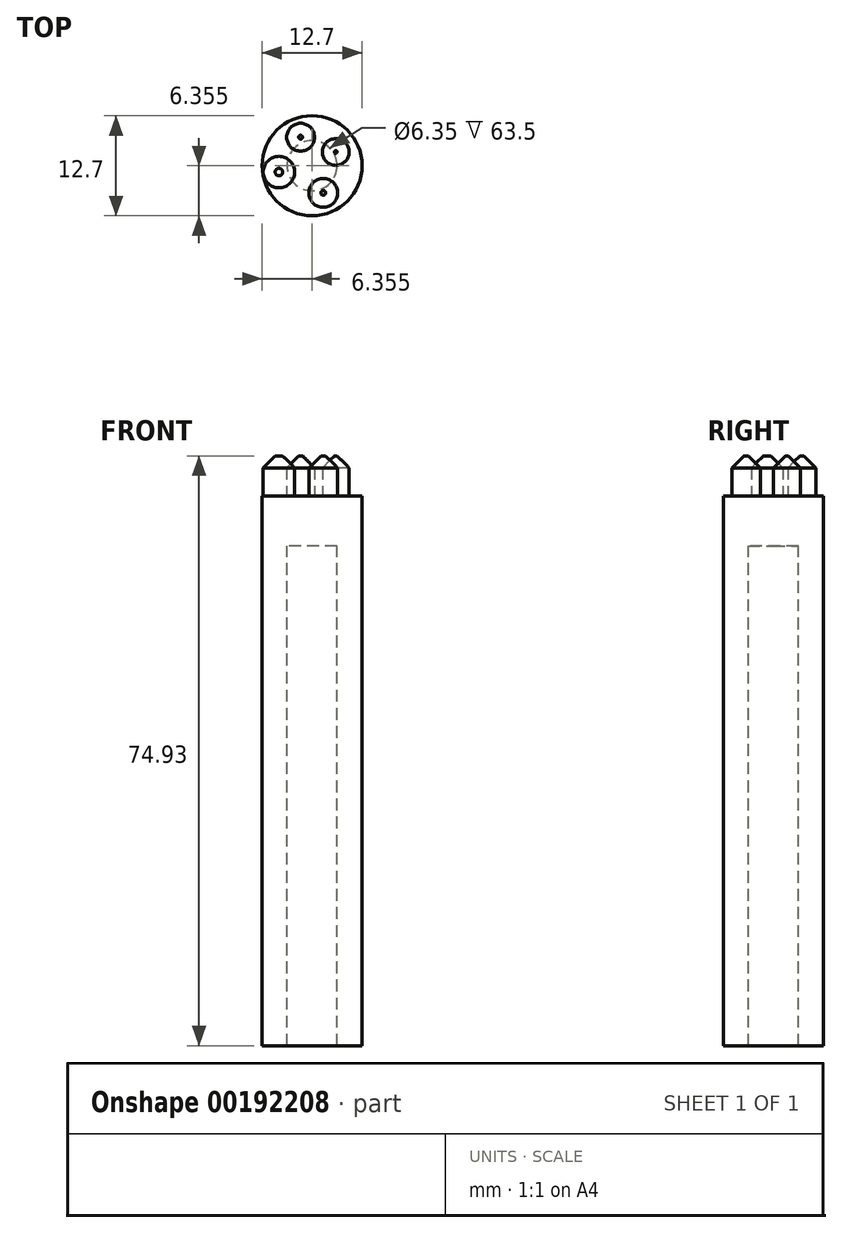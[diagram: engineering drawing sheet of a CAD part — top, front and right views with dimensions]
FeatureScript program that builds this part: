
annotation { "Feature Type Name" : "Feature", "Feature Type Description" : "" }
export const myFeature = defineFeature(function(context is Context, id is Id, definition is map)
    precondition{}
    {
        {
            var Q0;
            Q0=qCreatedBy(makeId("Top.planeOp"),FACE);
            var sketch = newSketch(context, id + "F0", { "sketchPlane" : qUnion([Q0])});
            skCircle(sketch, "E0", {"center": v(-23.02, -49.18) * mm, "radius": 6.35 * mm});
            skSolve(sketch);
        }
        {
            var Q0;
            Q0=makeQuery(id+"F0.imprint","IMPRINT",FACE,{"disambiguationData":[TD([[makeQuery(id+"F0.imprint","IMPRINT",EDGE,{"derivedFrom":sQuery(id+"F0.wireOp",EDGE,"E0")}),1.0]])]});
            extrude(context, id + "F1", {"entities" : qUnion([Q0]), "depth" : 63.5 * mm});
        }
        {
            var Q0;
            Q0=makeQuery(id+"F1.opExtrude","CAP_FACE",FACE,{"disambiguationData":[OSD([sQuery(id+"F0.wireOp",EDGE,"E0")])],"isStart":false});
            var sketch = newSketch(context, id + "F2", { "sketchPlane" : qUnion([Q0])});
            skCircle(sketch, "E1", {"center": v(-23.02, -49.18) * mm, "radius": 6.35 * mm});
            skSolve(sketch);
        }
        {
            var Q0;
            Q0=makeQuery(id+"F1.opExtrude","CAP_FACE",FACE,{"disambiguationData":[OSD([sQuery(id+"F0.wireOp",EDGE,"E0")])],"isStart":false});
            var sketch = newSketch(context, id + "F3", { "sketchPlane" : qUnion([Q0])});
            skSolve(sketch);
        }
        {
            var Q0;
            Q0=qSketchRegion(id+"F3",true);
            var Q1;
            Q1=makeQuery(id+"F3.imprint","IMPRINT",FACE,{"disambiguationData":[TD([[makeQuery(id+"F3.imprint","IMPRINT",EDGE,{"derivedFrom":makeQuery(id+"F1.opExtrude","CAP_EDGE",EDGE,{"disambiguationData":[OSD([sQuery(id+"F0.wireOp",EDGE,"E0")])],"isStart":false})}),1.0]])]});
            extrude(context, id + "F4", {"entities" : qUnion([Q0, Q1]), "operationType" : NewBodyOperationType.ADD, "depth" : 6.35 * mm});
        }
        {
            var Q0;
            Q0=sQuery(id+"F2.wireOp",VERTEX,"E1.center");
            var Q1;
            Q1=makeQuery(id+"F1.opExtrude","SWEPT_BODY",BODY,{"disambiguationData":[OSD([sQuery(id+"F0.wireOp",EDGE,"E0")])]});
            hole(context, id + "F5", {"style" : HoleStyle.SIMPLE, "endStyle" : HoleEndStyle.BLIND, "holeDiameter" : 6.35 * mm, "holeDepth" : 63.5 * mm, "startFromSketch" : true, "locations" : qUnion([Q0]), "scope" : qUnion([Q1])});
        }
        {
            var Q0;
            Q0=makeQuery(id+"F4.opExtrude","CAP_FACE",FACE,{"disambiguationData":[OSD([sQuery(id+"F0.wireOp",EDGE,"E0")])],"isStart":false});
            var sketch = newSketch(context, id + "F6", { "sketchPlane" : qUnion([Q0])});
            skCircle(sketch, "E2", {"center": v(-27.23, -49.98) * mm, "radius": 2 * mm});
            skCircle(sketch, "E3", {"center": v(-24.47, -45.55) * mm, "radius": 1.77 * mm});
            skCircle(sketch, "E4", {"center": v(-20.01, -47.44) * mm, "radius": 1.7 * mm});
            skCircle(sketch, "E5", {"center": v(-21.6, -52.63) * mm, "radius": 1.83 * mm});
            skSolve(sketch);
        }
        {
            var Q0;
            Q0=makeQuery(id+"F6.imprint","IMPRINT",FACE,{"disambiguationData":[TD([[makeQuery(id+"F6.imprint","IMPRINT",EDGE,{"derivedFrom":sQuery(id+"F6.wireOp",EDGE,"E3")}),1.0]])]});
            var Q1;
            Q1=makeQuery(id+"F6.imprint","IMPRINT",FACE,{"disambiguationData":[TD([[makeQuery(id+"F6.imprint","IMPRINT",EDGE,{"derivedFrom":sQuery(id+"F6.wireOp",EDGE,"E4")}),1.0]])]});
            var Q2;
            Q2=makeQuery(id+"F6.imprint","IMPRINT",FACE,{"disambiguationData":[TD([[makeQuery(id+"F6.imprint","IMPRINT",EDGE,{"derivedFrom":sQuery(id+"F6.wireOp",EDGE,"E5")}),1.0]])]});
            var Q3;
            Q3=makeQuery(id+"F6.imprint","IMPRINT",FACE,{"disambiguationData":[TD([[makeQuery(id+"F6.imprint","IMPRINT",EDGE,{"derivedFrom":sQuery(id+"F6.wireOp",EDGE,"E2")}),1.0]])]});
            extrude(context, id + "F7", {"entities" : qUnion([Q0, Q1, Q2, Q3]), "operationType" : NewBodyOperationType.ADD, "depth" : 5.08 * mm});
        }
        {
            var Q0;
            Q0=makeQuery(id+"F7.opExtrude","CAP_EDGE",EDGE,{"disambiguationData":[OSD([sQuery(id+"F6.wireOp",EDGE,"E2")])],"isStart":false});
            var Q1;
            Q1=makeQuery(id+"F7.opExtrude","CAP_EDGE",EDGE,{"disambiguationData":[OSD([sQuery(id+"F6.wireOp",EDGE,"E3")])],"isStart":false});
            var Q2;
            Q2=makeQuery(id+"F7.opExtrude","CAP_EDGE",EDGE,{"disambiguationData":[OSD([sQuery(id+"F6.wireOp",EDGE,"E4")])],"isStart":false});
            var Q3;
            Q3=makeQuery(id+"F7.opExtrude","CAP_EDGE",EDGE,{"disambiguationData":[OSD([sQuery(id+"F6.wireOp",EDGE,"E5")])],"isStart":false});
            chamfer(context, id + "F8", {"entities" : qUnion([Q0, Q1, Q2, Q3]), "width" : 1.52 * mm, "tangentPropagation" : true});
        }
    });
